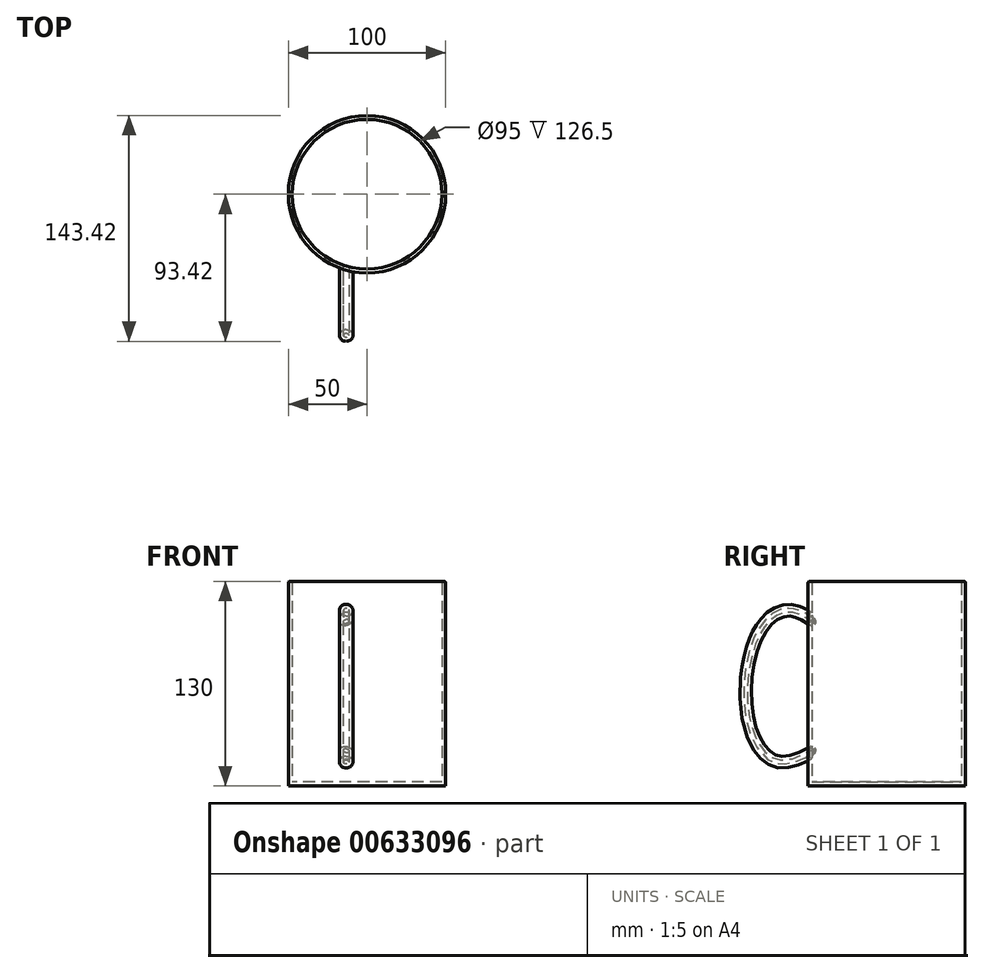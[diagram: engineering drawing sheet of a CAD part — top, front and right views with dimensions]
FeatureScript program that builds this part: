
annotation { "Feature Type Name" : "Feature", "Feature Type Description" : "" }
export const myFeature = defineFeature(function(context is Context, id is Id, definition is map)
    precondition{}
    {
        {
            var Q0;
            Q0=qCreatedBy(makeId("Top.planeOp"),FACE);
            var sketch = newSketch(context, id + "F0", { "sketchPlane" : qUnion([Q0])});
            skCircle(sketch, "E0", {"center": v(0, 0) * mm, "radius": 50 * mm});
            skSolve(sketch);
        }
        {
            var Q0;
            Q0=makeQuery(id+"F0.imprint","IMPRINT",FACE,{"disambiguationData":[TD([[makeQuery(id+"F0.imprint","IMPRINT",EDGE,{"derivedFrom":sQuery(id+"F0.wireOp",EDGE,"E0")}),1.0]])]});
            extrude(context, id + "F1", {"entities" : qUnion([Q0]), "depth" : 130 * mm, "offsetDistance" : 25 * mm});
        }
        {
            var Q0;
            Q0=qCreatedBy(makeId("Right.planeOp"),FACE);
            var sketch = newSketch(context, id + "F2", { "sketchPlane" : qUnion([Q0])});
            skFitSpline(sketch, "E1", {"points": [v(-43, 101.53) * mm, v(-61.79, 110.6) * mm, v(-79.5, 98.72) * mm, v(-87.7, 45.58) * mm, v(-70.21, 16.86) * mm, v(-41.27, 25.93) * mm], "startDerivative": vector(-113.92, 81.04) * mm, "endDerivative": vector(156.65, 87.52) * mm});
            skSolve(sketch);
        }
        {
            var Q0;
            Q0=qCreatedBy(makeId("Front.planeOp"),FACE);
            cPlane(context, id + "F3", {"entities" : qUnion([Q0]), "cplaneType" : CPlaneType.OFFSET, "offset" : 50 * mm, "width" : 150 * mm, "height" : 150 * mm});
        }
        {
            var Q0;
            Q0=qCreatedBy(id+"F3.planeOp",FACE);
            var sketch = newSketch(context, id + "F4", { "sketchPlane" : qUnion([Q0])});
            skCircle(sketch, "E2", {"center": v(-13.23, 107.39) * mm, "radius": 4.3 * mm});
            skSolve(sketch);
        }
        {
            var Q0;
            Q0=makeQuery(id+"F4.imprint","IMPRINT",FACE,{"disambiguationData":[TD([[makeQuery(id+"F4.imprint","IMPRINT",EDGE,{"derivedFrom":sQuery(id+"F4.wireOp",EDGE,"E2")}),1.0]])]});
            var Q1;
            Q1=sQuery(id+"F2.wireOp",EDGE,"E1");
            sweep(context, id + "F5", {"operationType" : NewBodyOperationType.ADD, "profiles" : qUnion([Q0]), "path" : qUnion([Q1])});
        }
        {
            var Q0;
            Q0=makeQuery(id+"F1.opExtrude","CAP_FACE",FACE,{"disambiguationData":[OSD([sQuery(id+"F0.wireOp",EDGE,"E0")])],"isStart":false});
            shell(context, id + "F6", {"entities" : qUnion([Q0]), "thickness" : 2.5 * mm});
        }
        {
            var Q0;
            Q0=makeQuery(id+"F1.opExtrude","CAP_EDGE",EDGE,{"disambiguationData":[OSD([sQuery(id+"F0.wireOp",EDGE,"E0")])],"isStart":false});
            fillet(context, id + "F7", {"entities" : qUnion([Q0]), "radius" : 1 * mm, "tangentPropagation" : true, "allowEdgeOverflow" : false});
        }
        {
            var Q0;
            {var subQ0=sQuery(id+"F0.wireOp",EDGE,"E0");Q0=makeQuery(id+"F6.opShell","OFFSET_EDGE",EDGE,{"disambiguationData":[OSD([subQ0]),TDD([makeQuery(id+"F1.opExtrude","CAP_EDGE",EDGE,{"disambiguationData":[OSD([subQ0])],"isStart":false})])]});}
            fillet(context, id + "F8", {"entities" : qUnion([Q0]), "radius" : 1 * mm, "tangentPropagation" : true, "allowEdgeOverflow" : false});
        }
    });
